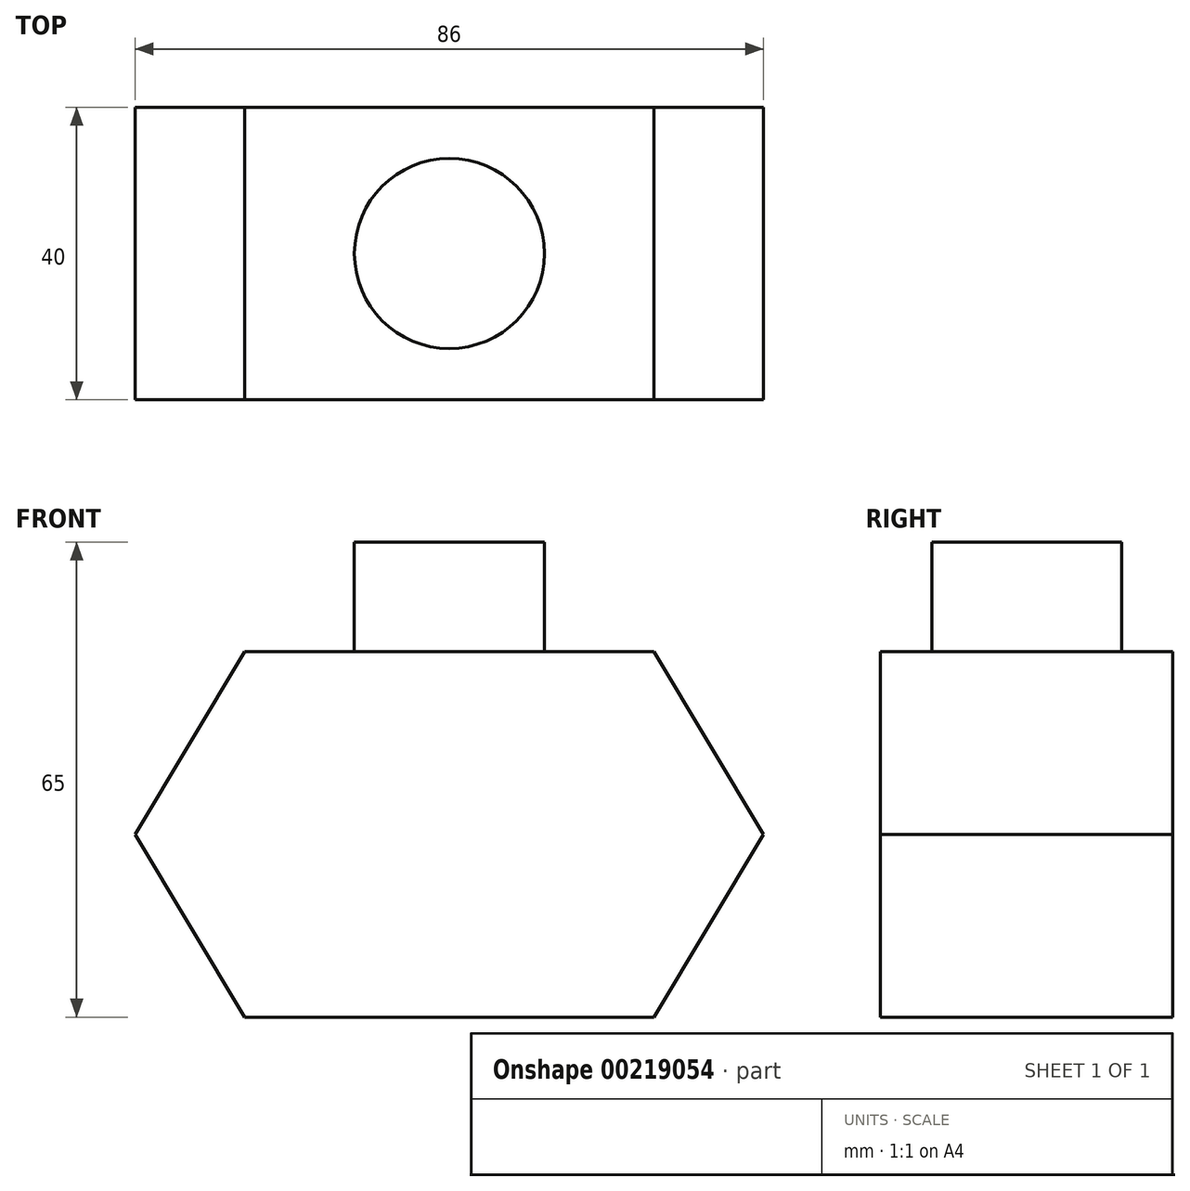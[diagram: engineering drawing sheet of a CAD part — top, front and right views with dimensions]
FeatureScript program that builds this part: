
annotation { "Feature Type Name" : "Feature", "Feature Type Description" : "" }
export const myFeature = defineFeature(function(context is Context, id is Id, definition is map)
    precondition{}
    {
        {
            var Q0;
            Q0=qCreatedBy(makeId("Front.planeOp"),FACE);
            var sketch = newSketch(context, id + "F0", { "sketchPlane" : qUnion([Q0])});
            skLineSegment(sketch, "E0", {"start": v(0, 0) * mm, "end": v(56, 0) * mm});
            skLineSegment(sketch, "E1", {"start": v(56, 0) * mm, "end": v(71, 25) * mm});
            skLineSegment(sketch, "E2", {"start": v(71, 25) * mm, "end": v(56, 50) * mm});
            skLineSegment(sketch, "E3", {"start": v(56, 50) * mm, "end": v(0, 50) * mm});
            skLineSegment(sketch, "E4", {"start": v(0, 50) * mm, "end": v(-15, 25) * mm});
            skLineSegment(sketch, "E5", {"start": v(-15, 25) * mm, "end": v(0, 0) * mm});
            skLineSegment(sketch, "E6", {"start": v(28, 50) * mm, "end": v(28, 65) * mm});
            skPoint(sketch, "E6.endSnap0", {"position": v(28, 50) * mm});
            skLineSegment(sketch, "E7", {"start": v(28, 65) * mm, "end": v(41, 65) * mm});
            skLineSegment(sketch, "E8", {"start": v(41, 65) * mm, "end": v(41, 50) * mm});
            skSolve(sketch);
        }
        {
            var Q0;
            Q0=makeQuery(id+"F0.imprint","IMPRINT",FACE,{"disambiguationData":[TD([[makeQuery(id+"F0.imprint","IMPRINT",EDGE,{"derivedFrom":sQuery(id+"F0.wireOp",EDGE,"E0")}),1.0]])]});
            extrude(context, id + "F1", {"entities" : qUnion([Q0]), "endBound" : BoundingType.SYMMETRIC, "depth" : 40 * mm});
        }
        {
            var Q0;
            {var subQ0=sQuery(id+"F0.wireOp",EDGE,"E6");Q0=makeQuery(id+"F0.imprint","IMPRINT",FACE,{"disambiguationData":[TD([[makeQuery(id+"F0.imprint","IMPRINT",EDGE,{"derivedFrom":subQ0}),-1.0]])]});}
            var Q1;
            Q1=sQuery(id+"F0.wireOp",EDGE,"E6");
            revolve(context, id + "F2", {"operationType" : NewBodyOperationType.ADD, "entities" : qUnion([Q0]), "axis" : qUnion([Q1]), "revolveType" : RevolveType.FULL});
        }
    });
